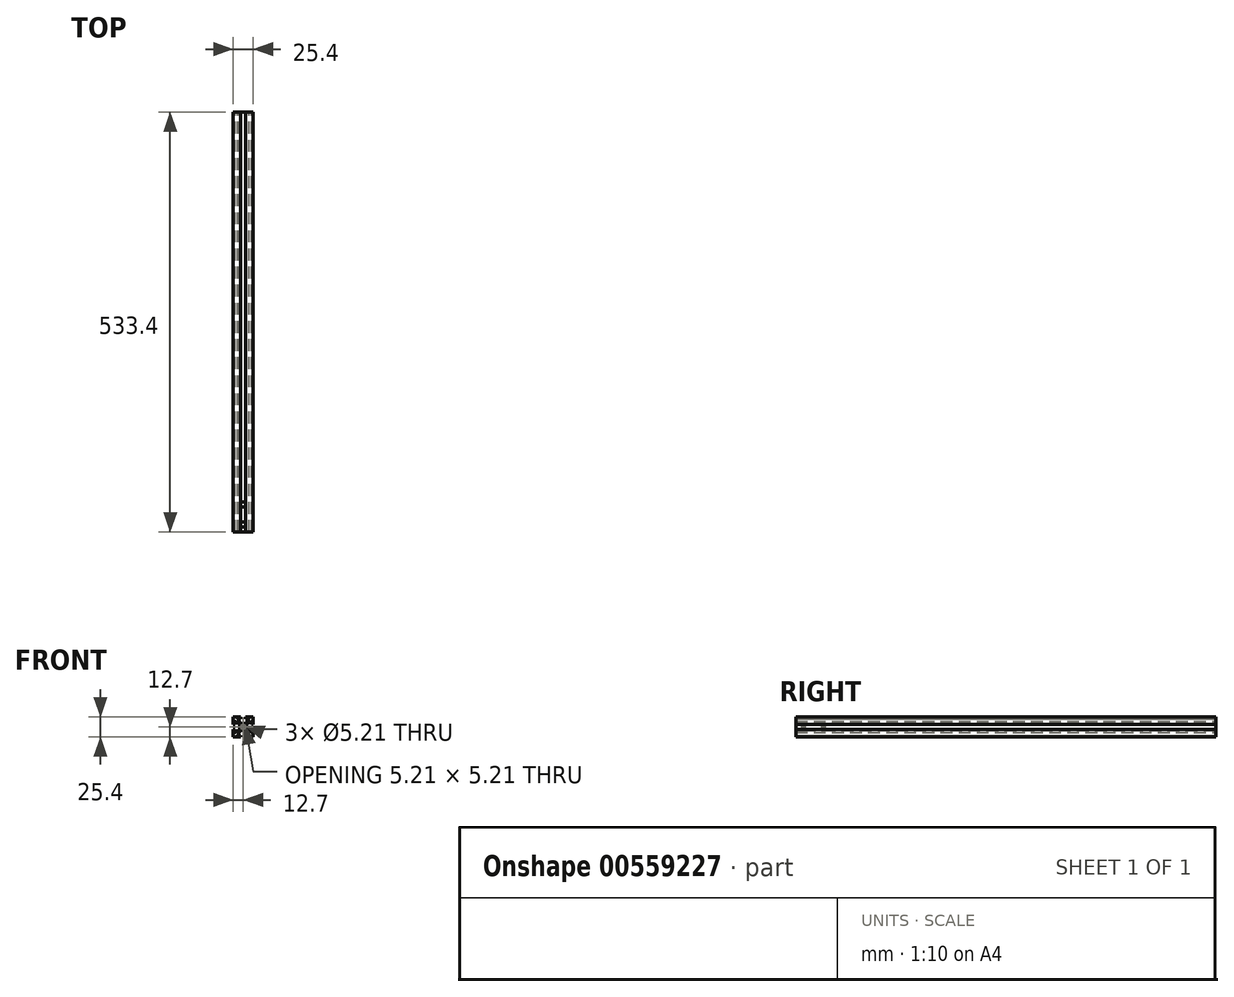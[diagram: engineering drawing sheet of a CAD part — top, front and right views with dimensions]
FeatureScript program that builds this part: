
annotation { "Feature Type Name" : "Feature", "Feature Type Description" : "" }
export const myFeature = defineFeature(function(context is Context, id is Id, definition is map)
    precondition{}
    {
        {
            var Q0;
            Q0=qCreatedBy(makeId("Front.planeOp"),FACE);
            var sketch = newSketch(context, id + "F0", { "sketchPlane" : qUnion([Q0])});
            skCircle(sketch, "E0", {"center": v(0, 0) * mm, "radius": 2.6 * mm});
            skLineSegment(sketch, "E1.bottom", {"start": v(-4.5, 4.5) * mm, "end": v(4.5, 4.5) * mm});
            skLineSegment(sketch, "E1.top", {"start": v(-4.5, -4.5) * mm, "end": v(4.5, -4.5) * mm});
            skLineSegment(sketch, "E1.left", {"start": v(-4.5, 4.5) * mm, "end": v(-4.5, -4.5) * mm});
            skLineSegment(sketch, "E1.right", {"start": v(4.5, 4.5) * mm, "end": v(4.5, -4.5) * mm});
            skLineSegment(sketch, "E2.bottom", {"start": v(-12.7, 12.7) * mm, "end": v(12.7, 12.7) * mm});
            skLineSegment(sketch, "E2.top", {"start": v(-12.7, -12.7) * mm, "end": v(12.7, -12.7) * mm});
            skLineSegment(sketch, "E2.left", {"start": v(-12.7, 12.7) * mm, "end": v(-12.7, -12.7) * mm});
            skLineSegment(sketch, "E2.right", {"start": v(12.7, 12.7) * mm, "end": v(12.7, -12.7) * mm});
            skLineSegment(sketch, "E3.bottom", {"start": v(-3.24, 12.7) * mm, "end": v(3.24, 12.7) * mm});
            skLineSegment(sketch, "E3.top", {"start": v(-3.24, 4.5) * mm, "end": v(3.24, 4.5) * mm});
            skLineSegment(sketch, "E3.left", {"start": v(-3.24, 12.7) * mm, "end": v(-3.24, 10.5) * mm});
            skLineSegment(sketch, "E3.right", {"start": v(3.24, 12.7) * mm, "end": v(3.24, 10.5) * mm});
            skLineSegment(sketch, "E4.bottom", {"start": v(-7.43, 10.5) * mm, "end": v(-3.24, 10.5) * mm});
            skLineSegment(sketch, "E5", {"start": v(-7.43, 10.5) * mm, "end": v(-3.24, 4.5) * mm});
            skLineSegment(sketch, "E6", {"start": v(3.24, 4.5) * mm, "end": v(7.43, 10.5) * mm});
            skLineSegment(sketch, "E7.trimOffspring", {"start": v(3.24, 10.5) * mm, "end": v(7.43, 10.5) * mm});
            skLineSegment(sketch, "E8.bottom", {"start": v(-12.7, 3.24) * mm, "end": v(-10.5, 3.24) * mm});
            skLineSegment(sketch, "E8.top", {"start": v(-12.7, -3.24) * mm, "end": v(-10.5, -3.24) * mm});
            skLineSegment(sketch, "E8.left", {"start": v(-12.7, 3.24) * mm, "end": v(-12.7, -3.24) * mm});
            skLineSegment(sketch, "E8.right", {"start": v(-4.5, 3.24) * mm, "end": v(-4.5, -3.24) * mm});
            skLineSegment(sketch, "E9.left", {"start": v(-10.5, 7.43) * mm, "end": v(-10.5, 3.24) * mm});
            skLineSegment(sketch, "E10", {"start": v(-10.5, 7.43) * mm, "end": v(-4.5, 3.24) * mm});
            skLineSegment(sketch, "E11.trimOffspring", {"start": v(-10.5, -3.24) * mm, "end": v(-10.5, -7.43) * mm});
            skLineSegment(sketch, "E12.MirrorCS", {"start": v(-3.24, -12.7) * mm, "end": v(-3.24, -10.5) * mm});
            skLineSegment(sketch, "E13.MirrorCS", {"start": v(-7.43, -10.5) * mm, "end": v(-3.24, -10.5) * mm});
            skLineSegment(sketch, "E14.MirrorCS", {"start": v(-7.43, -10.5) * mm, "end": v(-3.24, -4.5) * mm});
            skLineSegment(sketch, "E15.MirrorCS", {"start": v(3.24, -4.5) * mm, "end": v(7.43, -10.5) * mm});
            skLineSegment(sketch, "E16.MirrorCS", {"start": v(3.24, -10.5) * mm, "end": v(7.43, -10.5) * mm});
            skLineSegment(sketch, "E17.MirrorCS", {"start": v(3.24, -12.7) * mm, "end": v(3.24, -10.5) * mm});
            skLineSegment(sketch, "E18.MirrorCS", {"start": v(10.5, 7.43) * mm, "end": v(4.5, 3.24) * mm});
            skLineSegment(sketch, "E19.MirrorCS", {"start": v(10.5, -3.24) * mm, "end": v(10.5, -7.43) * mm});
            skLineSegment(sketch, "E20.MirrorCS", {"start": v(12.7, -3.24) * mm, "end": v(10.5, -3.24) * mm});
            skLineSegment(sketch, "E21.MirrorCS", {"start": v(12.7, 3.24) * mm, "end": v(10.5, 3.24) * mm});
            skLineSegment(sketch, "E22.MirrorCS", {"start": v(10.5, 7.43) * mm, "end": v(10.5, 3.24) * mm});
            skLineSegment(sketch, "E23", {"start": v(-10.5, -7.43) * mm, "end": v(-4.5, -3.24) * mm});
            skLineSegment(sketch, "E24", {"start": v(4.5, -3.24) * mm, "end": v(10.5, -7.43) * mm});
            skSolve(sketch);
        }
        {
            var Q0;
            {var subQ1=sQuery(id+"F0.wireOp",EDGE,"E3.left");Q0=makeQuery(id+"F0.imprint","IMPRINT",FACE,{"disambiguationData":[TD([[makeQuery(id+"F0.imprint","IMPRINT",EDGE,{"derivedFrom":subQ1}),-1.0]])]});}
            var Q1;
            {var subQ3=sQuery(id+"F0.wireOp",EDGE,"E3.right");Q1=makeQuery(id+"F0.imprint","IMPRINT",FACE,{"disambiguationData":[TD([[makeQuery(id+"F0.imprint","IMPRINT",EDGE,{"derivedFrom":subQ3}),1.0]])]});}
            var Q2;
            Q2=makeQuery(id+"F0.imprint","IMPRINT",FACE,{"disambiguationData":[TD([[makeQuery(id+"F0.imprint","IMPRINT",EDGE,{"derivedFrom":sQuery(id+"F0.wireOp",EDGE,"E0")}),-1.0]])]});
            var Q3;
            {var subQ0=sQuery(id+"F0.wireOp",EDGE,"E8.top");Q3=makeQuery(id+"F0.imprint","IMPRINT",FACE,{"disambiguationData":[TD([[makeQuery(id+"F0.imprint","IMPRINT",EDGE,{"derivedFrom":subQ0}),-1.0]])]});}
            var Q4;
            {var subQ9=sQuery(id+"F0.wireOp",EDGE,"E15.MirrorCS");Q4=makeQuery(id+"F0.imprint","IMPRINT",FACE,{"disambiguationData":[TD([[makeQuery(id+"F0.imprint","IMPRINT",EDGE,{"derivedFrom":subQ9}),1.0]])]});}
            extrude(context, id + "F1", {"entities" : qUnion([Q0, Q1, Q2, Q3, Q4]), "depth" : 533.4 * mm, "offsetDistance" : 25.4 * mm});
        }
        {
            var Q0;
            Q0=makeQuery(id+"F1.opExtrude","SWEPT_EDGE",EDGE,{"disambiguationData":[OSD([sQuery(id+"F0.wireOp",EDGE,"E4.bottom"),sQuery(id+"F0.wireOp",EDGE,"E5")])]});
            var Q1;
            Q1=makeQuery(id+"F1.opExtrude","SWEPT_EDGE",EDGE,{"disambiguationData":[OSD([sQuery(id+"F0.wireOp",EDGE,"E6"),sQuery(id+"F0.wireOp",EDGE,"E7.trimOffspring")])]});
            var Q2;
            Q2=makeQuery(id+"F1.opExtrude","SWEPT_EDGE",EDGE,{"disambiguationData":[OSD([sQuery(id+"F0.wireOp",EDGE,"E9.left"),sQuery(id+"F0.wireOp",EDGE,"E10")])]});
            var Q3;
            Q3=makeQuery(id+"F1.opExtrude","SWEPT_EDGE",EDGE,{"disambiguationData":[OSD([sQuery(id+"F0.wireOp",EDGE,"E11.trimOffspring"),sQuery(id+"F0.wireOp",EDGE,"E23")])]});
            var Q4;
            Q4=makeQuery(id+"F1.opExtrude","SWEPT_EDGE",EDGE,{"disambiguationData":[OSD([sQuery(id+"F0.wireOp",EDGE,"E13.MirrorCS"),sQuery(id+"F0.wireOp",EDGE,"E14.MirrorCS")])]});
            var Q5;
            Q5=makeQuery(id+"F1.opExtrude","SWEPT_EDGE",EDGE,{"disambiguationData":[OSD([sQuery(id+"F0.wireOp",EDGE,"E15.MirrorCS"),sQuery(id+"F0.wireOp",EDGE,"E16.MirrorCS")])]});
            var Q6;
            Q6=makeQuery(id+"F1.opExtrude","SWEPT_EDGE",EDGE,{"disambiguationData":[OSD([sQuery(id+"F0.wireOp",EDGE,"E19.MirrorCS"),sQuery(id+"F0.wireOp",EDGE,"E24")])]});
            var Q7;
            Q7=makeQuery(id+"F1.opExtrude","SWEPT_EDGE",EDGE,{"disambiguationData":[OSD([sQuery(id+"F0.wireOp",EDGE,"E18.MirrorCS"),sQuery(id+"F0.wireOp",EDGE,"E22.MirrorCS")])]});
            fillet(context, id + "F2", {"entities" : qUnion([Q0, Q1, Q2, Q3, Q4, Q5, Q6, Q7]), "radius" : 0.25 * mm, "tangentPropagation" : true, "allowEdgeOverflow" : false});
        }
        {
            var Q0;
            {var subQ0=sQuery(id+"F0.wireOp",EDGE,"E2.bottom");Q0=makeQuery(id+"F1.opExtrude","SWEPT_FACE",FACE,{"disambiguationData":[OSD([subQ0]),TDD([makeQuery(id+"F0.imprint","IMPRINT",EDGE,{"disambiguationData":[TD([[makeQuery(id+"F0.imprint","INTERSECT",VERTEX,{"derivedFrom":[subQ0,sQuery(id+"F0.wireOp",EDGE,"E2.left")]}),-1.0]])],"derivedFrom":subQ0})])]});}
            var sketch = newSketch(context, id + "F3", { "sketchPlane" : qUnion([Q0])});
            skLineSegment(sketch, "E25", {"start": v(-12.7, -523.96) * mm, "end": v(12.7, -523.96) * mm});
            skLineSegment(sketch, "E26", {"start": v(-12.7, -498.56) * mm, "end": v(12.7, -498.56) * mm});
            skCircle(sketch, "E27", {"center": v(0, -523.96) * mm, "radius": 3.26 * mm});
            skCircle(sketch, "E28", {"center": v(0, -498.56) * mm, "radius": 3.26 * mm});
            skSolve(sketch);
        }
        {
            var Q0;
            {var subQ0=sQuery(id+"F3.wireOp",EDGE,"E28");var subQ1=sQuery(id+"F3.wireOp",EDGE,"E26");var subQ2=makeQuery(id+"F3.imprint","INTERSECT",VERTEX,{"disambiguationData":[OD(0.0)],"derivedFrom":[subQ1,subQ0]});Q0=makeQuery(id+"F3.imprint","IMPRINT",FACE,{"disambiguationData":[TD([[makeQuery(id+"F3.imprint","IMPRINT",EDGE,{"disambiguationData":[TD([[subQ2,1.0]])],"derivedFrom":subQ1}),-1.0]])]});}
            var Q1;
            {var subQ0=sQuery(id+"F3.wireOp",EDGE,"E28");var subQ1=sQuery(id+"F3.wireOp",EDGE,"E26");var subQ2=makeQuery(id+"F3.imprint","INTERSECT",VERTEX,{"disambiguationData":[OD(0.0)],"derivedFrom":[subQ1,subQ0]});Q1=makeQuery(id+"F3.imprint","IMPRINT",FACE,{"disambiguationData":[TD([[makeQuery(id+"F3.imprint","IMPRINT",EDGE,{"disambiguationData":[TD([[subQ2,1.0]])],"derivedFrom":subQ1}),1.0]])]});}
            var Q2;
            {var subQ0=sQuery(id+"F3.wireOp",EDGE,"E27");var subQ1=sQuery(id+"F3.wireOp",EDGE,"E25");var subQ2=makeQuery(id+"F3.imprint","INTERSECT",VERTEX,{"disambiguationData":[OD(0.0)],"derivedFrom":[subQ1,subQ0]});Q2=makeQuery(id+"F3.imprint","IMPRINT",FACE,{"disambiguationData":[TD([[makeQuery(id+"F3.imprint","IMPRINT",EDGE,{"disambiguationData":[TD([[subQ2,1.0]])],"derivedFrom":subQ1}),-1.0]])]});}
            var Q3;
            {var subQ0=sQuery(id+"F3.wireOp",EDGE,"E27");var subQ1=sQuery(id+"F3.wireOp",EDGE,"E25");var subQ2=makeQuery(id+"F3.imprint","INTERSECT",VERTEX,{"disambiguationData":[OD(0.0)],"derivedFrom":[subQ1,subQ0]});Q3=makeQuery(id+"F3.imprint","IMPRINT",FACE,{"disambiguationData":[TD([[makeQuery(id+"F3.imprint","IMPRINT",EDGE,{"disambiguationData":[TD([[subQ2,1.0]])],"derivedFrom":subQ1}),1.0]])]});}
            extrude(context, id + "F4", {"entities" : qUnion([Q0, Q1, Q2, Q3]), "operationType" : NewBodyOperationType.REMOVE, "oppositeDirection" : true, "depth" : 25.4 * mm, "offsetDistance" : 25.4 * mm});
        }
    });
